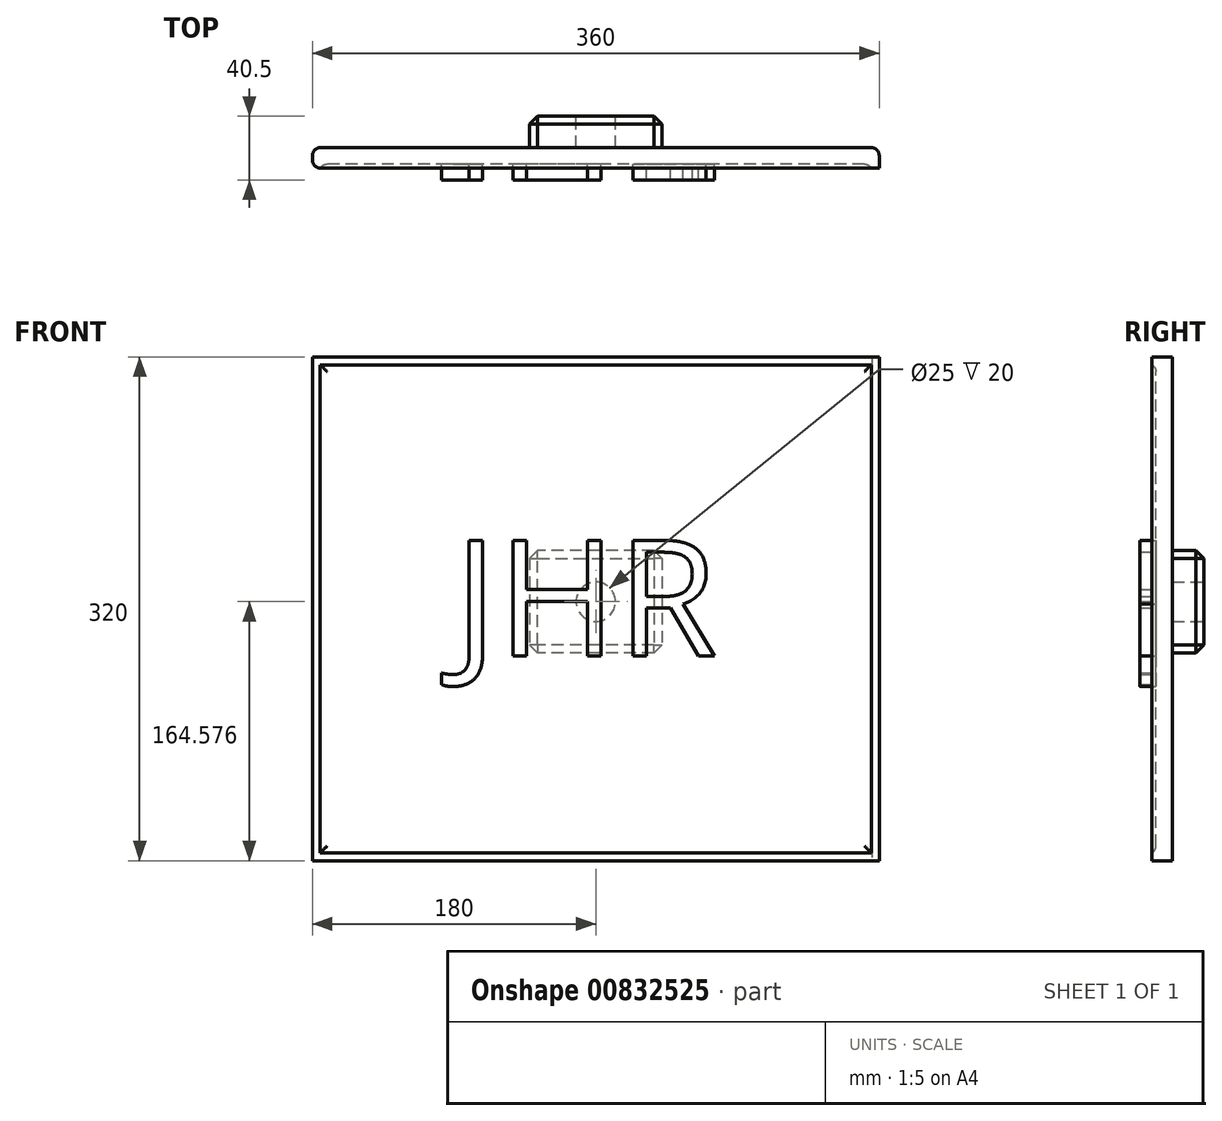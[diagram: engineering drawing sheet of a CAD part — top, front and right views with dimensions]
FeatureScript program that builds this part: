
annotation { "Feature Type Name" : "Feature", "Feature Type Description" : "" }
export const myFeature = defineFeature(function(context is Context, id is Id, definition is map)
    precondition{}
    {
        {
            var Q0;
            Q0=qCreatedBy(makeId("Top.planeOp"),FACE);
            var sketch = newSketch(context, id + "F0", { "sketchPlane" : qUnion([Q0])});
            skLineSegment(sketch, "E0.bottom", {"start": v(-175, 26.94) * mm, "end": v(180, 26.94) * mm});
            skLineSegment(sketch, "E0.top", {"start": v(-175, 13.94) * mm, "end": v(180, 13.94) * mm});
            skLineSegment(sketch, "E0.left", {"start": v(-180, 21.94) * mm, "end": v(-180, 18.94) * mm});
            skLineSegment(sketch, "E0.right", {"start": v(180, 21.97) * mm, "end": v(180, 13.94) * mm});
            skPoint(sketch, "E1.visualSharp", {"position": v(-180, 26.94) * mm});
            skArc(sketch, "E1.filletArc", {"start": v(-175, 26.94) * mm, "mid": v(-178.54, 25.48) * mm, "end": v(-180, 21.94) * mm});
            skPoint(sketch, "E2.visualSharp", {"position": v(180, 26.94) * mm});
            skArc(sketch, "E2.filletArc", {"start": v(180, 21.97) * mm, "mid": v(178.55, 25.49) * mm, "end": v(175.05, 26.97) * mm});
            skPoint(sketch, "E3.visualSharp", {"position": v(-180, 13.94) * mm});
            skArc(sketch, "E3.filletArc", {"start": v(-180, 18.94) * mm, "mid": v(-178.54, 15.4) * mm, "end": v(-175, 13.94) * mm});
            skSolve(sketch);
        }
        {
            var Q0;
            Q0 = qSketchRegion(id + "F0", true);
            extrude(context, id + "F1", {"entities" : qUnion([Q0]), "depth" : 320 * mm, "offsetDistance" : 25 * mm});
        }
        {
            var Q0;
            Q0=makeQuery(id+"F1.opExtrude","SWEPT_FACE",FACE,{"disambiguationData":[OSD([sQuery(id+"F0.wireOp",EDGE,"E0.top")])]});
            var sketch = newSketch(context, id + "F2", { "sketchPlane" : qUnion([Q0])});
            skLineSegment(sketch, "E4.bottom", {"start": v(-175, 315) * mm, "end": v(175, 315) * mm});
            skLineSegment(sketch, "E4.top", {"start": v(-175, 5) * mm, "end": v(175, 5) * mm});
            skLineSegment(sketch, "E4.left", {"start": v(-175, 315) * mm, "end": v(-175, 5) * mm});
            skLineSegment(sketch, "E4.right", {"start": v(175, 315) * mm, "end": v(175, 5) * mm});
            skSolve(sketch);
        }
        {
            var Q0;
            Q0=makeQuery(id+"F2.imprint","IMPRINT",FACE,{"disambiguationData":[TD([[makeQuery(id+"F2.imprint","IMPRINT",EDGE,{"derivedFrom":sQuery(id+"F2.wireOp",EDGE,"E4.bottom")}),-1.0]])]});
            extrude(context, id + "F3", {"entities" : qUnion([Q0]), "operationType" : NewBodyOperationType.REMOVE, "oppositeDirection" : true, "depth" : 2.5 * mm, "offsetDistance" : 25 * mm});
        }
        {
            var Q0;
            Q0=makeQuery(id+"F1.opExtrude","SWEPT_FACE",FACE,{"disambiguationData":[OSD([sQuery(id+"F0.wireOp",EDGE,"E0.bottom")])]});
            var sketch = newSketch(context, id + "F4", { "sketchPlane" : qUnion([Q0])});
            skLineSegment(sketch, "E5.bottom", {"start": v(-42, 197.08) * mm, "end": v(42, 197.08) * mm});
            skLineSegment(sketch, "E5.top", {"start": v(-42, 132.08) * mm, "end": v(42, 132.08) * mm});
            skLineSegment(sketch, "E5.left", {"start": v(-42, 197.08) * mm, "end": v(-42, 132.08) * mm});
            skLineSegment(sketch, "E5.right", {"start": v(42, 197.08) * mm, "end": v(42, 132.08) * mm});
            skSolve(sketch);
        }
        {
            var Q0;
            Q0=makeQuery(id+"F4.imprint","IMPRINT",FACE,{"disambiguationData":[TD([[makeQuery(id+"F4.imprint","IMPRINT",EDGE,{"derivedFrom":sQuery(id+"F4.wireOp",EDGE,"E5.bottom")}),-1.0]])]});
            extrude(context, id + "F5", {"entities" : qUnion([Q0]), "operationType" : NewBodyOperationType.ADD, "depth" : 20 * mm, "offsetDistance" : 25 * mm});
        }
        {
            var Q0;
            Q0=makeQuery(id+"F5.opExtrude","CAP_EDGE",EDGE,{"disambiguationData":[OSD([sQuery(id+"F4.wireOp",EDGE,"E5.bottom")])],"isStart":false});
            var Q1;
            Q1=makeQuery(id+"F5.opExtrude","CAP_EDGE",EDGE,{"disambiguationData":[OSD([sQuery(id+"F4.wireOp",EDGE,"E5.left")])],"isStart":false});
            var Q2;
            Q2=makeQuery(id+"F5.opExtrude","CAP_EDGE",EDGE,{"disambiguationData":[OSD([sQuery(id+"F4.wireOp",EDGE,"E5.top")])],"isStart":false});
            var Q3;
            Q3=makeQuery(id+"F5.opExtrude","CAP_EDGE",EDGE,{"disambiguationData":[OSD([sQuery(id+"F4.wireOp",EDGE,"E5.right")])],"isStart":false});
            var Q4;
            Q4=makeQuery(id+"F5.opExtrude","SWEPT_EDGE",EDGE,{"disambiguationData":[OSD([sQuery(id+"F4.wireOp",EDGE,"E5.bottom"),sQuery(id+"F4.wireOp",EDGE,"E5.left")])]});
            var Q5;
            Q5=makeQuery(id+"F5.opExtrude","SWEPT_EDGE",EDGE,{"disambiguationData":[OSD([sQuery(id+"F4.wireOp",EDGE,"E5.top"),sQuery(id+"F4.wireOp",EDGE,"E5.left")])]});
            var Q6;
            Q6=makeQuery(id+"F5.opExtrude","SWEPT_EDGE",EDGE,{"disambiguationData":[OSD([sQuery(id+"F4.wireOp",EDGE,"E5.top"),sQuery(id+"F4.wireOp",EDGE,"E5.right")])]});
            var Q7;
            Q7=makeQuery(id+"F5.opExtrude","SWEPT_EDGE",EDGE,{"disambiguationData":[OSD([sQuery(id+"F4.wireOp",EDGE,"E5.bottom"),sQuery(id+"F4.wireOp",EDGE,"E5.right")])]});
            chamfer(context, id + "F6", {"entities" : qUnion([Q0, Q1, Q2, Q3, Q4, Q5, Q6, Q7]), "width" : 5 * mm, "tangentPropagation" : true});
        }
        {
            var Q0;
            Q0=makeQuery(id+"F3.boolean.opBoolean","COPY",FACE,{"derivedFrom":makeQuery(id+"F3.opExtrude","CAP_FACE",FACE,{"disambiguationData":[OSD([sQuery(id+"F2.wireOp",EDGE,"E4.bottom"),sQuery(id+"F2.wireOp",EDGE,"E4.top"),sQuery(id+"F2.wireOp",EDGE,"E4.left"),sQuery(id+"F2.wireOp",EDGE,"E4.right")])],"isStart":false})});
            fillet(context, id + "F7", {"entities" : qUnion([Q0]), "radius" : 5 * mm, "tangentPropagation" : true, "allowEdgeOverflow" : false});
        }
        {
            var Q0;
            Q0=makeQuery(id+"F5.opExtrude","CAP_FACE",FACE,{"disambiguationData":[OSD([sQuery(id+"F4.wireOp",EDGE,"E5.bottom"),sQuery(id+"F4.wireOp",EDGE,"E5.top"),sQuery(id+"F4.wireOp",EDGE,"E5.left"),sQuery(id+"F4.wireOp",EDGE,"E5.right")])],"isStart":false});
            var sketch = newSketch(context, id + "F8", { "sketchPlane" : qUnion([Q0])});
            skCircle(sketch, "E6", {"center": v(0, 164.58) * mm, "radius": 12.5 * mm});
            skPoint(sketch, "E6.centerSnap0", {"position": v(-37, 164.58) * mm});
            skSolve(sketch);
        }
        {
            var Q0;
            Q0=makeQuery(id+"F8.imprint","IMPRINT",FACE,{"disambiguationData":[TD([[makeQuery(id+"F8.imprint","IMPRINT",EDGE,{"derivedFrom":sQuery(id+"F8.wireOp",EDGE,"E6")}),1.0]])]});
            var Q1;
            Q1=sQuery(id+"F8.wireOp",EDGE,"E6");
            extrude(context, id + "F9", {"entities" : qUnion([Q0]), "operationType" : NewBodyOperationType.REMOVE, "surfaceEntities" : qUnion([Q1]), "oppositeDirection" : true, "depth" : 20 * mm, "offsetDistance" : 25 * mm});
        }
        {
            var Q0;
            Q0=makeQuery(id+"F3.boolean.opBoolean","COPY",FACE,{"derivedFrom":makeQuery(id+"F3.opExtrude","CAP_FACE",FACE,{"disambiguationData":[OSD([sQuery(id+"F2.wireOp",EDGE,"E4.bottom"),sQuery(id+"F2.wireOp",EDGE,"E4.top"),sQuery(id+"F2.wireOp",EDGE,"E4.left"),sQuery(id+"F2.wireOp",EDGE,"E4.right")])],"isStart":false})});
            var sketch = newSketch(context, id + "F10", { "sketchPlane" : qUnion([Q0])});
            skText(sketch, "E7", { "text": "JHR", "fontName": "OpenSans-Regular.ttf"});
            const initialGuessF10  = {"E7": [-0.09, 0.13002, 1, 0, 0.0741]};
            skSetInitialGuess(sketch, initialGuessF10);
            skSolve(sketch);
        }
        {
            var Q0;
            Q0 = qSketchRegion(id + "F10", true);
            extrude(context, id + "F11", {"entities" : qUnion([Q0]), "operationType" : NewBodyOperationType.ADD, "depth" : 10 * mm, "offsetDistance" : 25 * mm});
        }
    });
